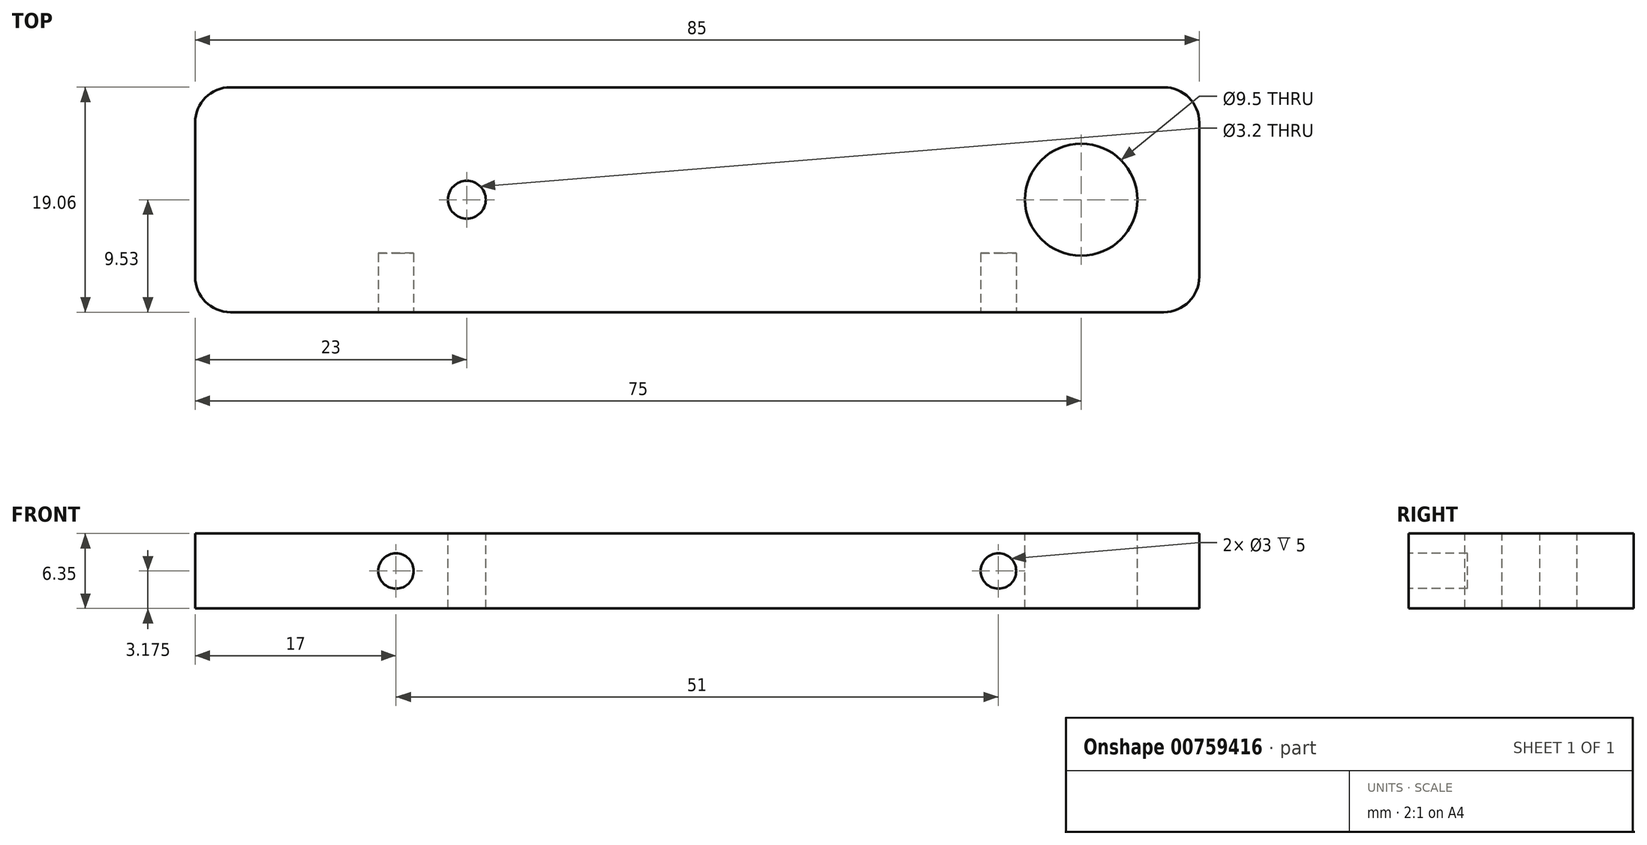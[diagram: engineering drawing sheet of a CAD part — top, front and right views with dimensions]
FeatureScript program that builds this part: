
annotation { "Feature Type Name" : "Feature", "Feature Type Description" : "" }
export const myFeature = defineFeature(function(context is Context, id is Id, definition is map)
    precondition{}
    {
        {
            var Q0;
            Q0=qCreatedBy(makeId("Top.planeOp"),FACE);
            var sketch = newSketch(context, id + "F0", { "sketchPlane" : qUnion([Q0])});
            skLineSegment(sketch, "E0.bottom", {"start": v(42.5, -9.53) * mm, "end": v(-42.5, -9.53) * mm});
            skLineSegment(sketch, "E0.top", {"start": v(42.5, 9.53) * mm, "end": v(-42.5, 9.52) * mm});
            skLineSegment(sketch, "E0.left", {"start": v(42.5, -9.52) * mm, "end": v(42.5, 9.53) * mm});
            skLineSegment(sketch, "E0.right", {"start": v(-42.5, -9.53) * mm, "end": v(-42.5, 9.52) * mm});
            skPoint(sketch, "E0.middle", {"position": v(0, 0) * mm});
            skSolve(sketch);
        }
        {
            var Q0;
            Q0 = qSketchRegion(id + "F0", true);
            extrude(context, id + "F1", {"entities" : qUnion([Q0]), "depth" : 6.35 * mm, "offsetDistance" : 25 * mm});
        }
        {
            var Q0;
            Q0=makeQuery(id+"F1.opExtrude","SWEPT_FACE",FACE,{"disambiguationData":[OSD([sQuery(id+"F0.wireOp",EDGE,"E0.bottom")])]});
            var sketch = newSketch(context, id + "F2", { "sketchPlane" : qUnion([Q0])});
            skCircle(sketch, "E1", {"center": v(-25.5, 3.17) * mm, "radius": 1.5 * mm});
            skCircle(sketch, "E2", {"center": v(25.5, 3.17) * mm, "radius": 1.5 * mm});
            skSolve(sketch);
        }
        {
            var Q0;
            Q0=makeQuery(id+"F2.imprint","IMPRINT",FACE,{"disambiguationData":[TD([[makeQuery(id+"F2.imprint","IMPRINT",EDGE,{"derivedFrom":sQuery(id+"F2.wireOp",EDGE,"E1")}),1.0]])]});
            extrude(context, id + "F3", {"entities" : qUnion([Q0]), "operationType" : NewBodyOperationType.REMOVE, "oppositeDirection" : true, "depth" : 5 * mm, "offsetDistance" : 25 * mm});
        }
        {
            var Q0;
            Q0=makeQuery(id+"F2.imprint","IMPRINT",FACE,{"disambiguationData":[TD([[makeQuery(id+"F2.imprint","IMPRINT",EDGE,{"derivedFrom":sQuery(id+"F2.wireOp",EDGE,"E2")}),1.0]])]});
            extrude(context, id + "F4", {"entities" : qUnion([Q0]), "operationType" : NewBodyOperationType.REMOVE, "oppositeDirection" : true, "depth" : 5 * mm, "offsetDistance" : 25 * mm});
        }
        {
            var Q0;
            Q0=makeQuery(id+"F1.opExtrude","SWEPT_EDGE",EDGE,{"disambiguationData":[OSD([sQuery(id+"F0.wireOp",EDGE,"E0.top"),sQuery(id+"F0.wireOp",EDGE,"E0.right")])]});
            fillet(context, id + "F5", {"entities" : qUnion([Q0]), "radius" : 3 * mm, "tangentPropagation" : true, "allowEdgeOverflow" : false});
        }
        {
            var Q0;
            Q0=makeQuery(id+"F1.opExtrude","SWEPT_EDGE",EDGE,{"disambiguationData":[OSD([sQuery(id+"F0.wireOp",EDGE,"E0.bottom"),sQuery(id+"F0.wireOp",EDGE,"E0.right")])]});
            fillet(context, id + "F6", {"entities" : qUnion([Q0]), "radius" : 3 * mm, "tangentPropagation" : true, "allowEdgeOverflow" : false});
        }
        {
            var Q0;
            Q0=makeQuery(id+"F1.opExtrude","SWEPT_EDGE",EDGE,{"disambiguationData":[OSD([sQuery(id+"F0.wireOp",EDGE,"E0.top"),sQuery(id+"F0.wireOp",EDGE,"E0.left")])]});
            var Q1;
            Q1=makeQuery(id+"F1.opExtrude","SWEPT_EDGE",EDGE,{"disambiguationData":[OSD([sQuery(id+"F0.wireOp",EDGE,"E0.bottom"),sQuery(id+"F0.wireOp",EDGE,"E0.left")])]});
            fillet(context, id + "F7", {"entities" : qUnion([Q0, Q1]), "radius" : 3 * mm, "tangentPropagation" : true, "allowEdgeOverflow" : false});
        }
        {
            var Q0;
            Q0=makeQuery(id+"F1.opExtrude","CAP_FACE",FACE,{"disambiguationData":[OSD([sQuery(id+"F0.wireOp",EDGE,"E0.bottom"),sQuery(id+"F0.wireOp",EDGE,"E0.top"),sQuery(id+"F0.wireOp",EDGE,"E0.left"),sQuery(id+"F0.wireOp",EDGE,"E0.right")])],"isStart":false});
            var sketch = newSketch(context, id + "F8", { "sketchPlane" : qUnion([Q0])});
            skCircle(sketch, "E3", {"center": v(32.5, 0) * mm, "radius": 4.75 * mm});
            skCircle(sketch, "E4", {"center": v(-19.5, 0) * mm, "radius": 1.6 * mm});
            skSolve(sketch);
        }
        {
            var Q0;
            Q0=makeQuery(id+"F8.imprint","IMPRINT",FACE,{"disambiguationData":[TD([[makeQuery(id+"F8.imprint","IMPRINT",EDGE,{"derivedFrom":sQuery(id+"F8.wireOp",EDGE,"E4")}),1.0]])]});
            var Q1;
            Q1=makeQuery(id+"F8.imprint","IMPRINT",FACE,{"disambiguationData":[TD([[makeQuery(id+"F8.imprint","IMPRINT",EDGE,{"derivedFrom":sQuery(id+"F8.wireOp",EDGE,"E3")}),1.0]])]});
            extrude(context, id + "F9", {"entities" : qUnion([Q0, Q1]), "operationType" : NewBodyOperationType.REMOVE, "oppositeDirection" : true, "depth" : 25 * mm, "offsetDistance" : 25 * mm});
        }
    });
